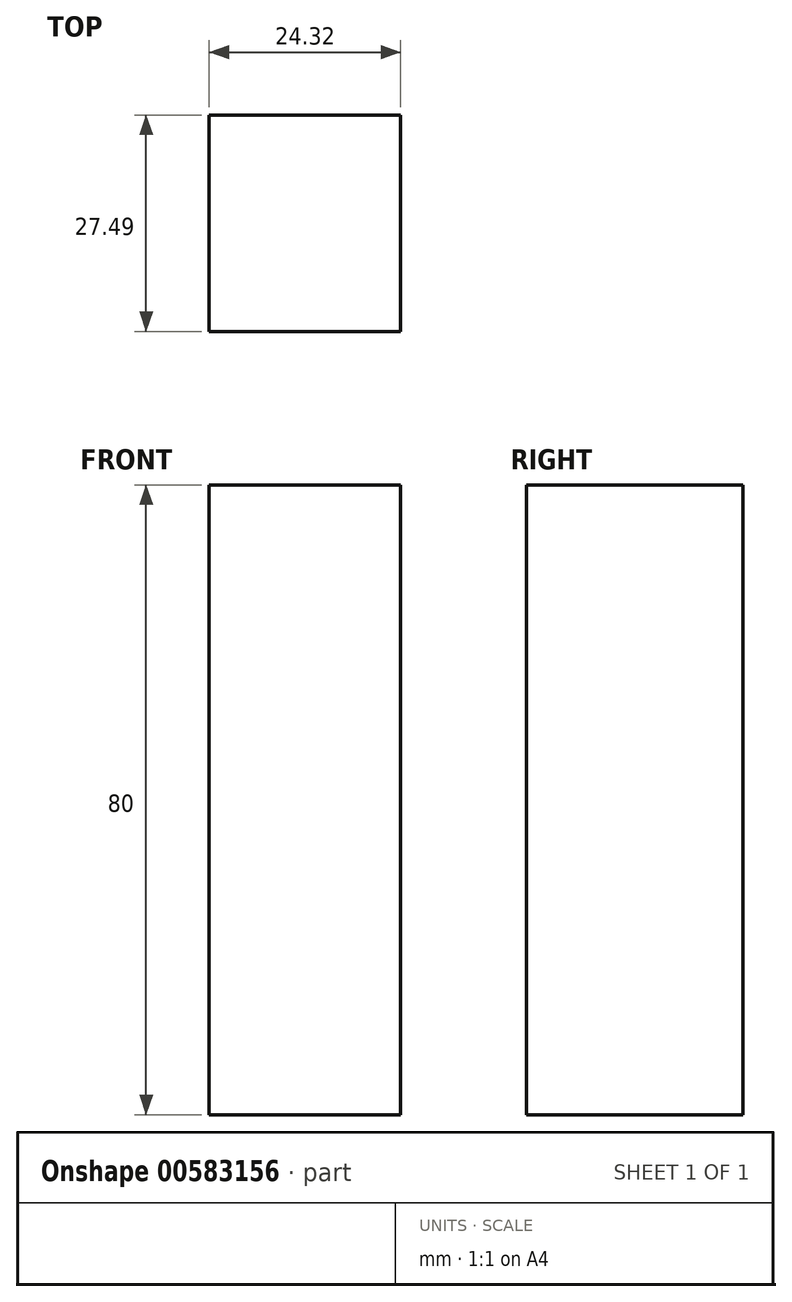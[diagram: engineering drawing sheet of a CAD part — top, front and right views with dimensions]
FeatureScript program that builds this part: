
annotation { "Feature Type Name" : "Feature", "Feature Type Description" : "" }
export const myFeature = defineFeature(function(context is Context, id is Id, definition is map)
    precondition{}
    {
        {
            var Q0;
            Q0=qCreatedBy(makeId("Top.planeOp"),FACE);
            var sketch = newSketch(context, id + "F0", { "sketchPlane" : qUnion([Q0])});
            skLineSegment(sketch, "E0.bottom", {"start": v(0, 0) * mm, "end": v(-24.32, 0) * mm});
            skLineSegment(sketch, "E0.top", {"start": v(0, 27.49) * mm, "end": v(-24.32, 27.49) * mm});
            skLineSegment(sketch, "E0.left", {"start": v(0, 0) * mm, "end": v(0, 27.49) * mm});
            skLineSegment(sketch, "E0.right", {"start": v(-24.32, 0) * mm, "end": v(-24.32, 27.49) * mm});
            skSolve(sketch);
        }
        {
            var Q0;
            Q0=makeQuery(id+"F0.imprint","IMPRINT",FACE,{"disambiguationData":[TD([[makeQuery(id+"F0.imprint","IMPRINT",EDGE,{"derivedFrom":sQuery(id+"F0.wireOp",EDGE,"E0.bottom")}),-1.0]])]});
            extrude(context, id + "F1", {"entities" : qUnion([Q0]), "depth" : 80 * mm, "offsetDistance" : 25 * mm});
        }
    });
